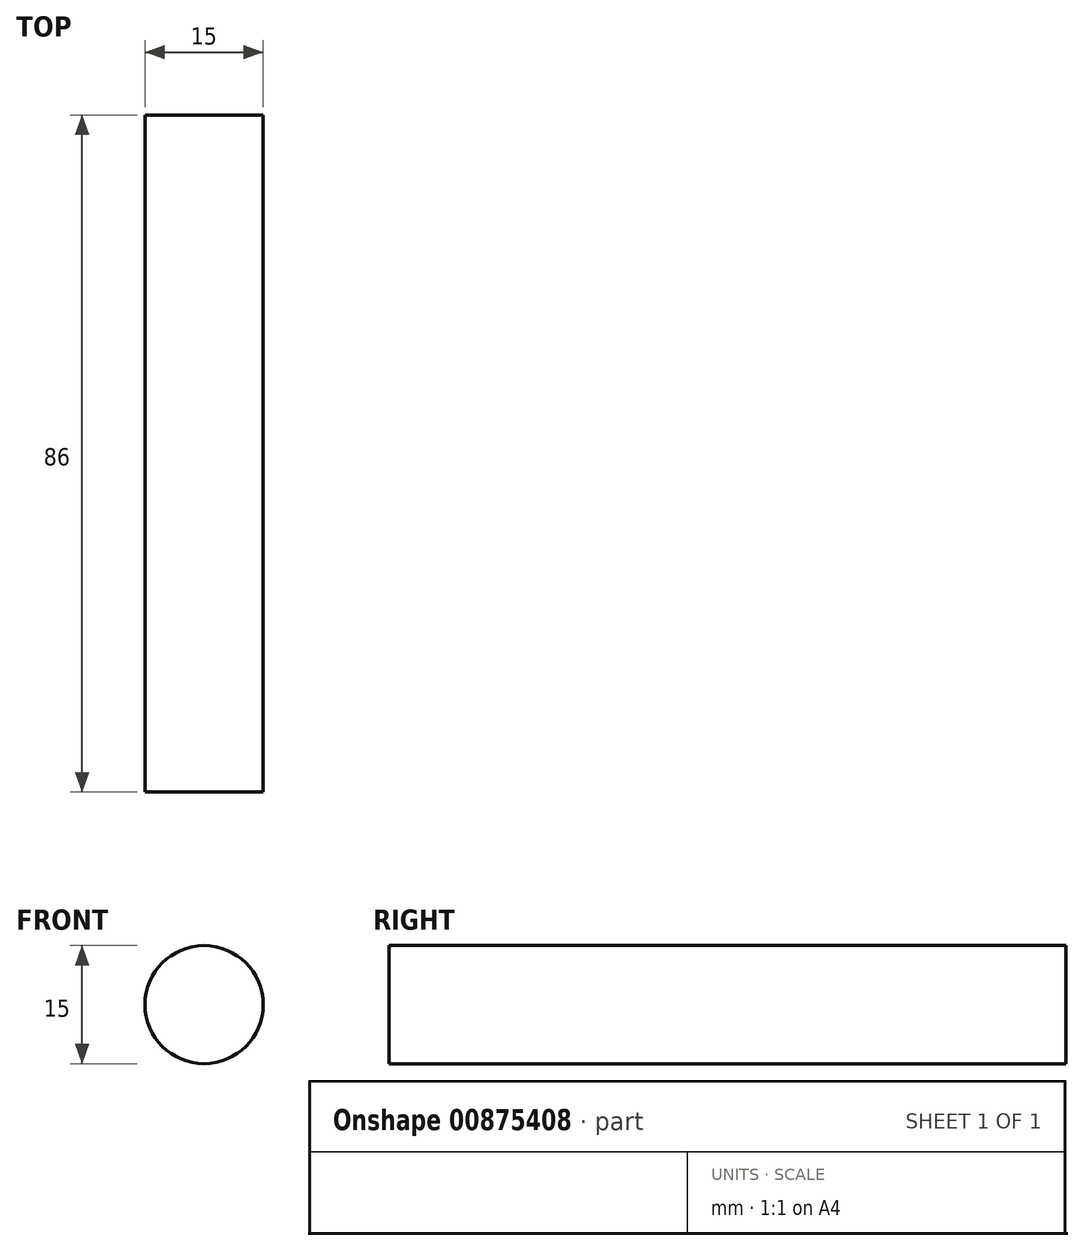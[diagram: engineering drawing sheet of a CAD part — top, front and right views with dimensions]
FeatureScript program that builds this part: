
annotation { "Feature Type Name" : "Feature", "Feature Type Description" : "" }
export const myFeature = defineFeature(function(context is Context, id is Id, definition is map)
    precondition{}
    {
        {
            var Q0;
            Q0=qCreatedBy(makeId("Front.planeOp"),FACE);
            var sketch = newSketch(context, id + "F0", { "sketchPlane" : qUnion([Q0])});
            skCircle(sketch, "E0", {"center": v(0, 0) * mm, "radius": 7.5 * mm});
            skSolve(sketch);
        }
        {
            var Q0;
            Q0 = qSketchRegion(id + "F0", true);
            extrude(context, id + "F1", {"entities" : qUnion([Q0]), "depth" : 86 * mm, "offsetDistance" : 25 * mm});
        }
    });
